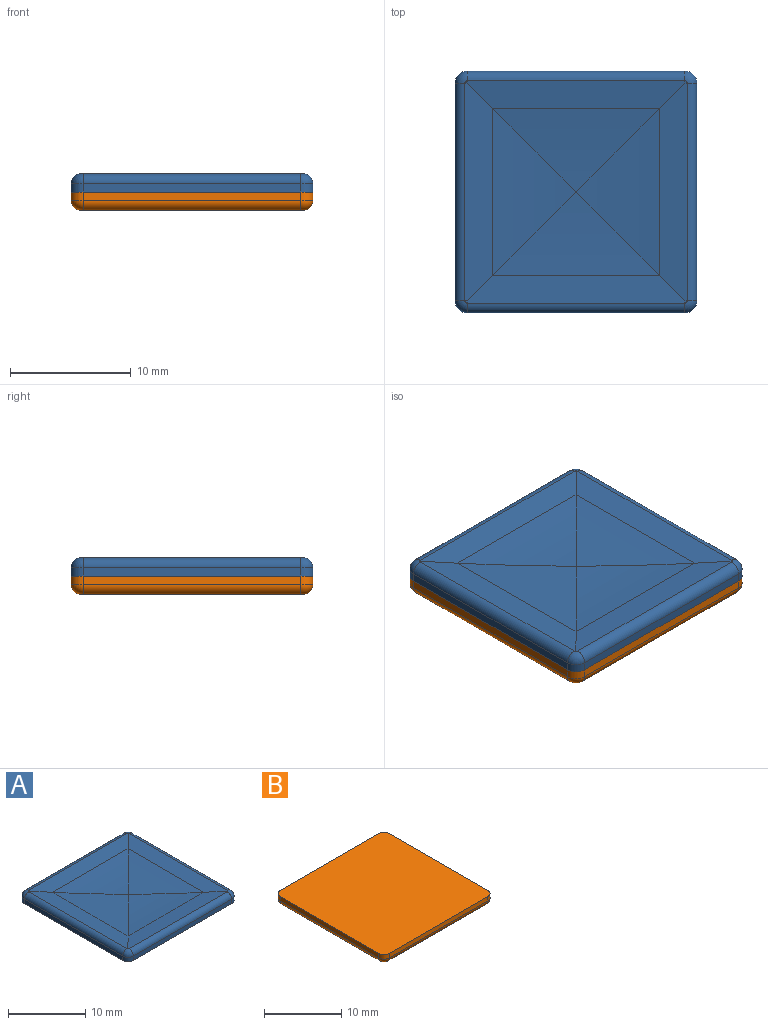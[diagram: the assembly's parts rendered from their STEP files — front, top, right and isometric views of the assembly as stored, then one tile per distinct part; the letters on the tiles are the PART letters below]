
ASSEMBLY  parts=2 mates=1
PART A: 30 faces, bbox 20x20x1.5 mm
  f0: plane 18x0.7mm, normal (1,0,0), area 12.6mm2, adj f1,f7,f8,f16
  f1: cylinder r=1mm len=1mm, axis (0,0,-1), area 1.1mm2, adj f0,f2,f8,f14
  f2: plane 18x0.7mm, normal (0,1,0), area 12.6mm2, adj f1,f3,f8,f12
  f3: cylinder r=1mm len=1mm, axis (0,0,-1), area 1.1mm2, adj f2,f4,f8,f10
  f4: plane 18x0.7mm, normal (-1,0,0), area 12.6mm2, adj f3,f5,f8,f9
  f5: cylinder r=1mm len=1mm, axis (0,0,-1), area 1.1mm2, adj f4,f6,f8,f11
  f6: plane 18x0.7mm, normal (0,-1,0), area 12.6mm2, adj f5,f7,f8,f13
  f7: cylinder r=1mm len=1mm, axis (0,0,-1), area 1.1mm2, adj f0,f6,f8,f15
  f8: plane 20x20mm, normal (0,0,-1), area 399.1mm2, adj f0,f1,f2,f3,f4,f5,f6,f7
  f9: cylinder r=0.8mm len=18mm, axis (0,1,0), area 22.6mm2, adj f4,f10,f11,f22
  f10: torus R=0.2mm, axis (0,0,1), area 1.4mm2, adj f3,f9,f12,f21
  f11: torus R=0.2mm, axis (0,0,1), area 1.4mm2, adj f5,f9,f13,f23
  f12: cylinder r=0.8mm len=18mm, axis (1,0,0), area 22.6mm2, adj f2,f10,f14,f20
  f13: cylinder r=0.8mm len=18mm, axis (-1,0,0), area 22.6mm2, adj f6,f11,f15,f24
  f14: torus R=0.2mm, axis (0,0,1), area 1.4mm2, adj f1,f12,f16,f19
  f15: torus R=0.2mm, axis (0,0,1), area 1.4mm2, adj f7,f13,f16,f17
  f16: cylinder r=0.8mm len=18mm, axis (0,-1,0), area 22.6mm2, adj f0,f14,f15,f18
  f17: cone r=0.2mm half-angle=85deg, axis (0,0,1), area 0mm2, adj f15,f18,f24
  f18: plane 18x2.28mm, normal (-0.09,0,1), area 36.8mm2, adj f16,f17,f19,f20,f24,f26
  f19: cone r=0.2mm half-angle=85deg, axis (0,0,1), area 0mm2, adj f14,f18,f20
  f20: plane 18x2.28mm, normal (0,-0.09,1), area 36.8mm2, adj f12,f18,f19,f21,f22,f27
  f21: cone r=0.2mm half-angle=85deg, axis (0,0,1), area 0mm2, adj f10,f20,f22
  f22: plane 18x2.28mm, normal (0.09,0,1), area 36.8mm2, adj f9,f20,f21,f23,f24,f29
  f23: cone r=0.2mm half-angle=85deg, axis (0,0,1), area 0mm2, adj f11,f22,f24
  f24: plane 18x2.28mm, normal (0,0.09,1), area 36.8mm2, adj f13,f17,f18,f22,f23,f28
  f25: plane 0.07x0.07mm, normal (0,0,1), area 0mm2, adj f26,f27,f28,f29
  f26: cylinder r=79mm len=13.84mm, axis (0,1,0), area 48mm2, adj f18,f25,f27,f28
  f27: cylinder r=79mm len=13.84mm, axis (-1,0,0), area 48mm2, adj f20,f25,f26,f29
  f28: cylinder r=79mm len=13.84mm, axis (1,0,0), area 48mm2, adj f24,f25,f26,f29
  f29: cylinder r=79mm len=13.84mm, axis (0,-1,0), area 48mm2, adj f22,f25,f27,f28
PART B: 30 faces, bbox 20x20x1.5 mm
  f0: plane 18x0.7mm, normal (1,0,0), area 12.6mm2, adj f1,f7,f8,f16
  f1: cylinder r=1mm len=1mm, axis (0,0,1), area 1.1mm2, adj f0,f2,f8,f14
  f2: plane 18x0.7mm, normal (0,1,0), area 12.6mm2, adj f1,f3,f8,f12
  f3: cylinder r=1mm len=1mm, axis (0,0,1), area 1.1mm2, adj f2,f4,f8,f10
  f4: plane 18x0.7mm, normal (-1,0,0), area 12.6mm2, adj f3,f5,f8,f9
  f5: cylinder r=1mm len=1mm, axis (0,0,1), area 1.1mm2, adj f4,f6,f8,f11
  f6: plane 18x0.7mm, normal (0,-1,0), area 12.6mm2, adj f5,f7,f8,f13
  f7: cylinder r=1mm len=1mm, axis (0,0,1), area 1.1mm2, adj f0,f6,f8,f15
  f8: plane 20x20mm, normal (0,0,1), area 399.1mm2, adj f0,f1,f2,f3,f4,f5,f6,f7
  f9: cylinder r=0.8mm len=18mm, axis (0,1,0), area 22.6mm2, adj f4,f10,f11,f22
  f10: torus R=0.2mm, axis (0,0,-1), area 1.4mm2, adj f3,f9,f12,f21
  f11: torus R=0.2mm, axis (0,0,-1), area 1.4mm2, adj f5,f9,f13,f23
  f12: cylinder r=0.8mm len=18mm, axis (1,0,0), area 22.6mm2, adj f2,f10,f14,f20
  f13: cylinder r=0.8mm len=18mm, axis (-1,0,0), area 22.6mm2, adj f6,f11,f15,f24
  f14: torus R=0.2mm, axis (0,0,-1), area 1.4mm2, adj f1,f12,f16,f19
  f15: torus R=0.2mm, axis (0,0,-1), area 1.4mm2, adj f7,f13,f16,f17
  f16: cylinder r=0.8mm len=18mm, axis (0,-1,0), area 22.6mm2, adj f0,f14,f15,f18
  f17: cone r=0.2mm half-angle=85deg, axis (0,0,-1), area 0mm2, adj f15,f18,f24
  f18: plane 18x2.28mm, normal (-0.09,0,-1), area 36.8mm2, adj f16,f17,f19,f20,f24,f26
  f19: cone r=0.2mm half-angle=85deg, axis (0,0,-1), area 0mm2, adj f14,f18,f20
  f20: plane 18x2.28mm, normal (0,-0.09,-1), area 36.8mm2, adj f12,f18,f19,f21,f22,f27
  f21: cone r=0.2mm half-angle=85deg, axis (0,0,-1), area 0mm2, adj f10,f20,f22
  f22: plane 18x2.28mm, normal (0.09,0,-1), area 36.8mm2, adj f9,f20,f21,f23,f24,f29
  f23: cone r=0.2mm half-angle=85deg, axis (0,0,-1), area 0mm2, adj f11,f22,f24
  f24: plane 18x2.28mm, normal (0,0.09,-1), area 36.8mm2, adj f13,f17,f18,f22,f23,f28
  f25: plane 0.07x0.07mm, normal (0,0,-1), area 0mm2, adj f26,f27,f28,f29
  f26: cylinder r=79mm len=13.84mm, axis (0,1,0), area 48mm2, adj f18,f25,f27,f28
  f27: cylinder r=79mm len=13.84mm, axis (-1,0,0), area 48mm2, adj f20,f25,f26,f29
  f28: cylinder r=79mm len=13.84mm, axis (1,0,0), area 48mm2, adj f24,f25,f26,f29
  f29: cylinder r=79mm len=13.84mm, axis (0,-1,0), area 48mm2, adj f22,f25,f27,f28
PLACE A at identity
PLACE B at identity
MATE fastened A.f8 <-> B.f8  axis (0,0,-1) through (-77,77,1.6)mm
